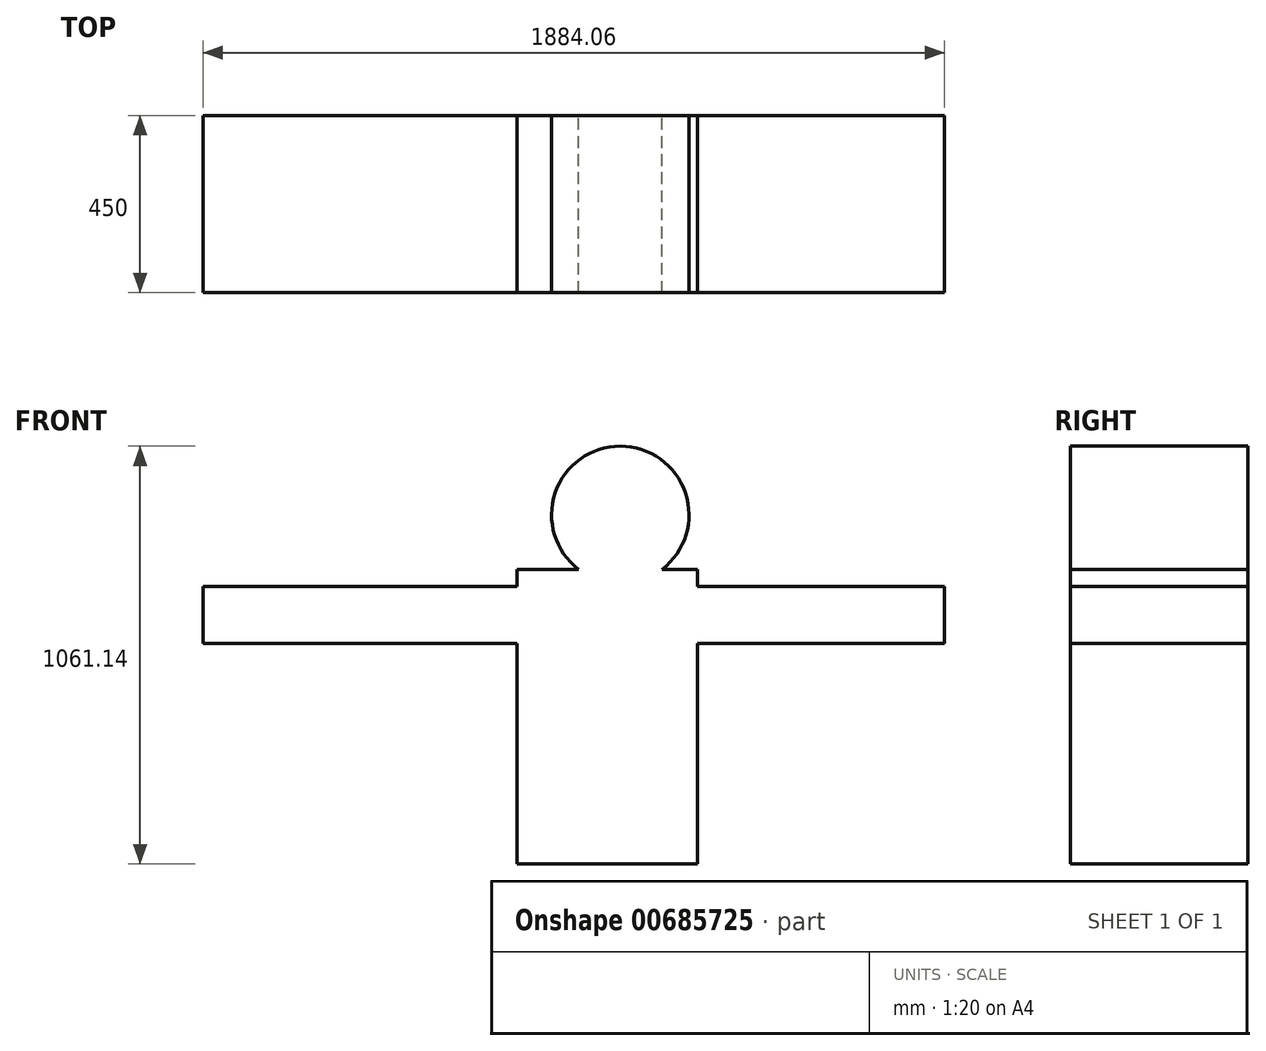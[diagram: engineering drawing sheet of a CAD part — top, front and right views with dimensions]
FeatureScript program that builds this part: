
annotation { "Feature Type Name" : "Feature", "Feature Type Description" : "" }
export const myFeature = defineFeature(function(context is Context, id is Id, definition is map)
    precondition{}
    {
        {
            var Q0;
            Q0=qCreatedBy(makeId("Front.planeOp"),FACE);
            var sketch = newSketch(context, id + "F0", { "sketchPlane" : qUnion([Q0])});
            skLineSegment(sketch, "E0.bottom", {"start": v(400, -846.22) * mm, "end": v(-400, -846.22) * mm});
            skLineSegment(sketch, "E0.top", {"start": v(400, 953.78) * mm, "end": v(-400, 953.78) * mm});
            skLineSegment(sketch, "E0.left", {"start": v(400, -846.22) * mm, "end": v(400, 953.78) * mm});
            skLineSegment(sketch, "E0.right", {"start": v(-400, -846.22) * mm, "end": v(-400, 953.78) * mm});
            skPoint(sketch, "E0.middle", {"position": v(0, 53.78) * mm});
            skCircle(sketch, "E1", {"center": v(0, 774.9) * mm, "radius": 174.52 * mm});
            skPoint(sketch, "E1.centerSnap0", {"position": v(0, 953.78) * mm});
            skLineSegment(sketch, "E2.bottom", {"start": v(-99.7, -846.22) * mm, "end": v(-235.16, -846.22) * mm});
            skLineSegment(sketch, "E2.top", {"start": v(-99.7, -71.7) * mm, "end": v(-235.16, -71.7) * mm});
            skLineSegment(sketch, "E2.left", {"start": v(-99.7, -846.22) * mm, "end": v(-99.7, -71.7) * mm});
            skLineSegment(sketch, "E2.right", {"start": v(-235.16, -846.22) * mm, "end": v(-235.16, -71.7) * mm});
            skLineSegment(sketch, "E3.bottom", {"start": v(0, -846.22) * mm, "end": v(165.05, -846.22) * mm});
            skLineSegment(sketch, "E3.top", {"start": v(0, -71.7) * mm, "end": v(165.05, -71.7) * mm});
            skLineSegment(sketch, "E3.left", {"start": v(0, -846.22) * mm, "end": v(0, -71.7) * mm});
            skLineSegment(sketch, "E3.right", {"start": v(165.05, -846.22) * mm, "end": v(165.05, -71.7) * mm});
            skLineSegment(sketch, "E4.bottom", {"start": v(-219.76, 593.26) * mm, "end": v(-1060.2, 593.26) * mm});
            skLineSegment(sketch, "E4.top", {"start": v(-219.76, 448.57) * mm, "end": v(-1060.2, 448.57) * mm});
            skLineSegment(sketch, "E4.left", {"start": v(-219.76, 593.26) * mm, "end": v(-219.76, 448.57) * mm});
            skLineSegment(sketch, "E4.right", {"start": v(-1060.2, 593.26) * mm, "end": v(-1060.2, 448.57) * mm});
            skPoint(sketch, "E5.oppositeSnap0", {"position": v(-639.98, 448.57) * mm});
            skLineSegment(sketch, "E5.bottom", {"start": v(137.35, 593.26) * mm, "end": v(823.86, 593.26) * mm});
            skLineSegment(sketch, "E5.top", {"start": v(137.35, 448.57) * mm, "end": v(823.86, 448.57) * mm});
            skLineSegment(sketch, "E5.left", {"start": v(137.35, 593.26) * mm, "end": v(137.35, 448.57) * mm});
            skLineSegment(sketch, "E5.right", {"start": v(823.86, 593.26) * mm, "end": v(823.86, 448.57) * mm});
            skLineSegment(sketch, "E6.bottom", {"start": v(-262.86, 636.36) * mm, "end": v(195.84, 636.36) * mm});
            skLineSegment(sketch, "E6.top", {"start": v(-262.86, -111.72) * mm, "end": v(195.84, -111.72) * mm});
            skLineSegment(sketch, "E6.left", {"start": v(-262.86, 636.36) * mm, "end": v(-262.86, -111.72) * mm});
            skLineSegment(sketch, "E6.right", {"start": v(195.84, 636.36) * mm, "end": v(195.84, -111.72) * mm});
            skSolve(sketch);
        }
        {
            var Q0;
            {var subQ0=sQuery(id+"F0.wireOp",EDGE,"E4.top");var subQ1=sQuery(id+"F0.wireOp",EDGE,"E0.right");var subQ2=makeQuery(id+"F0.imprint","INTERSECT",VERTEX,{"derivedFrom":[subQ1,subQ0]});Q0=makeQuery(id+"F0.imprint","IMPRINT",FACE,{"disambiguationData":[TD([[makeQuery(id+"F0.imprint","IMPRINT",EDGE,{"disambiguationData":[TD([[subQ2,-1.0]])],"derivedFrom":subQ1}),-1.0]])]});}
            var Q1;
            {var subQ5=sQuery(id+"F0.wireOp",EDGE,"E4.right");Q1=makeQuery(id+"F0.imprint","IMPRINT",FACE,{"disambiguationData":[TD([[makeQuery(id+"F0.imprint","IMPRINT",EDGE,{"derivedFrom":subQ5}),1.0]])]});}
            var Q2;
            {var subQ0=sQuery(id+"F0.wireOp",EDGE,"E4.left");Q2=makeQuery(id+"F0.imprint","IMPRINT",FACE,{"disambiguationData":[TD([[makeQuery(id+"F0.imprint","IMPRINT",EDGE,{"derivedFrom":subQ0}),-1.0]])]});}
            var Q3;
            {var subQ21=sQuery(id+"F0.wireOp",EDGE,"E2.top");Q3=makeQuery(id+"F0.imprint","IMPRINT",FACE,{"disambiguationData":[TD([[makeQuery(id+"F0.imprint","IMPRINT",EDGE,{"derivedFrom":subQ21}),-1.0]])]});}
            var Q4;
            {var subQ0=sQuery(id+"F0.wireOp",EDGE,"E6.bottom");var subQ1=sQuery(id+"F0.wireOp",EDGE,"E1");var subQ2=makeQuery(id+"F0.imprint","INTERSECT",VERTEX,{"disambiguationData":[OD(0.0)],"derivedFrom":[subQ1,subQ0]});Q4=makeQuery(id+"F0.imprint","IMPRINT",FACE,{"disambiguationData":[TD([[makeQuery(id+"F0.imprint","IMPRINT",EDGE,{"disambiguationData":[TD([[subQ2,1.0]])],"derivedFrom":subQ1}),1.0]])]});}
            var Q5;
            {var subQ0=sQuery(id+"F0.wireOp",EDGE,"E5.left");Q5=makeQuery(id+"F0.imprint","IMPRINT",FACE,{"disambiguationData":[TD([[makeQuery(id+"F0.imprint","IMPRINT",EDGE,{"derivedFrom":subQ0}),1.0]])]});}
            var Q6;
            {var subQ0=sQuery(id+"F0.wireOp",EDGE,"E5.top");var subQ1=sQuery(id+"F0.wireOp",EDGE,"E0.left");var subQ2=makeQuery(id+"F0.imprint","INTERSECT",VERTEX,{"derivedFrom":[subQ1,subQ0]});Q6=makeQuery(id+"F0.imprint","IMPRINT",FACE,{"disambiguationData":[TD([[makeQuery(id+"F0.imprint","IMPRINT",EDGE,{"disambiguationData":[TD([[subQ2,-1.0]])],"derivedFrom":subQ1}),1.0]])]});}
            var Q7;
            {var subQ0=sQuery(id+"F0.wireOp",EDGE,"E3.bottom");Q7=makeQuery(id+"F0.imprint","IMPRINT",FACE,{"disambiguationData":[TD([[makeQuery(id+"F0.imprint","IMPRINT",EDGE,{"derivedFrom":subQ0}),1.0]])]});}
            var Q8;
            {var subQ0=sQuery(id+"F0.wireOp",EDGE,"E2.bottom");Q8=makeQuery(id+"F0.imprint","IMPRINT",FACE,{"disambiguationData":[TD([[makeQuery(id+"F0.imprint","IMPRINT",EDGE,{"derivedFrom":subQ0}),-1.0]])]});}
            var Q9;
            {var subQ5=sQuery(id+"F0.wireOp",EDGE,"E5.right");Q9=makeQuery(id+"F0.imprint","IMPRINT",FACE,{"disambiguationData":[TD([[makeQuery(id+"F0.imprint","IMPRINT",EDGE,{"derivedFrom":subQ5}),-1.0]])]});}
            var Q10;
            {var subQ0=sQuery(id+"F0.wireOp",EDGE,"E6.bottom");var subQ1=sQuery(id+"F0.wireOp",EDGE,"E1");var subQ2=makeQuery(id+"F0.imprint","INTERSECT",VERTEX,{"disambiguationData":[OD(0.0)],"derivedFrom":[subQ1,subQ0]});Q10=makeQuery(id+"F0.imprint","IMPRINT",FACE,{"disambiguationData":[TD([[makeQuery(id+"F0.imprint","IMPRINT",EDGE,{"disambiguationData":[TD([[subQ2,-1.0]])],"derivedFrom":subQ1}),1.0]])]});}
            var Q11;
            {var subQ0=sQuery(id+"F0.wireOp",EDGE,"E3.top");Q11=makeQuery(id+"F0.imprint","IMPRINT",FACE,{"disambiguationData":[TD([[makeQuery(id+"F0.imprint","IMPRINT",EDGE,{"derivedFrom":subQ0}),-1.0]])]});}
            var Q12;
            {var subQ0=sQuery(id+"F0.wireOp",EDGE,"E2.top");Q12=makeQuery(id+"F0.imprint","IMPRINT",FACE,{"disambiguationData":[TD([[makeQuery(id+"F0.imprint","IMPRINT",EDGE,{"derivedFrom":subQ0}),1.0]])]});}
            extrude(context, id + "F1", {"entities" : qUnion([Q0, Q1, Q2, Q3, Q4, Q5, Q6, Q7, Q8, Q9, Q10, Q11, Q12]), "depth" : 450 * mm, "offsetDistance" : 25 * mm});
        }
    });
